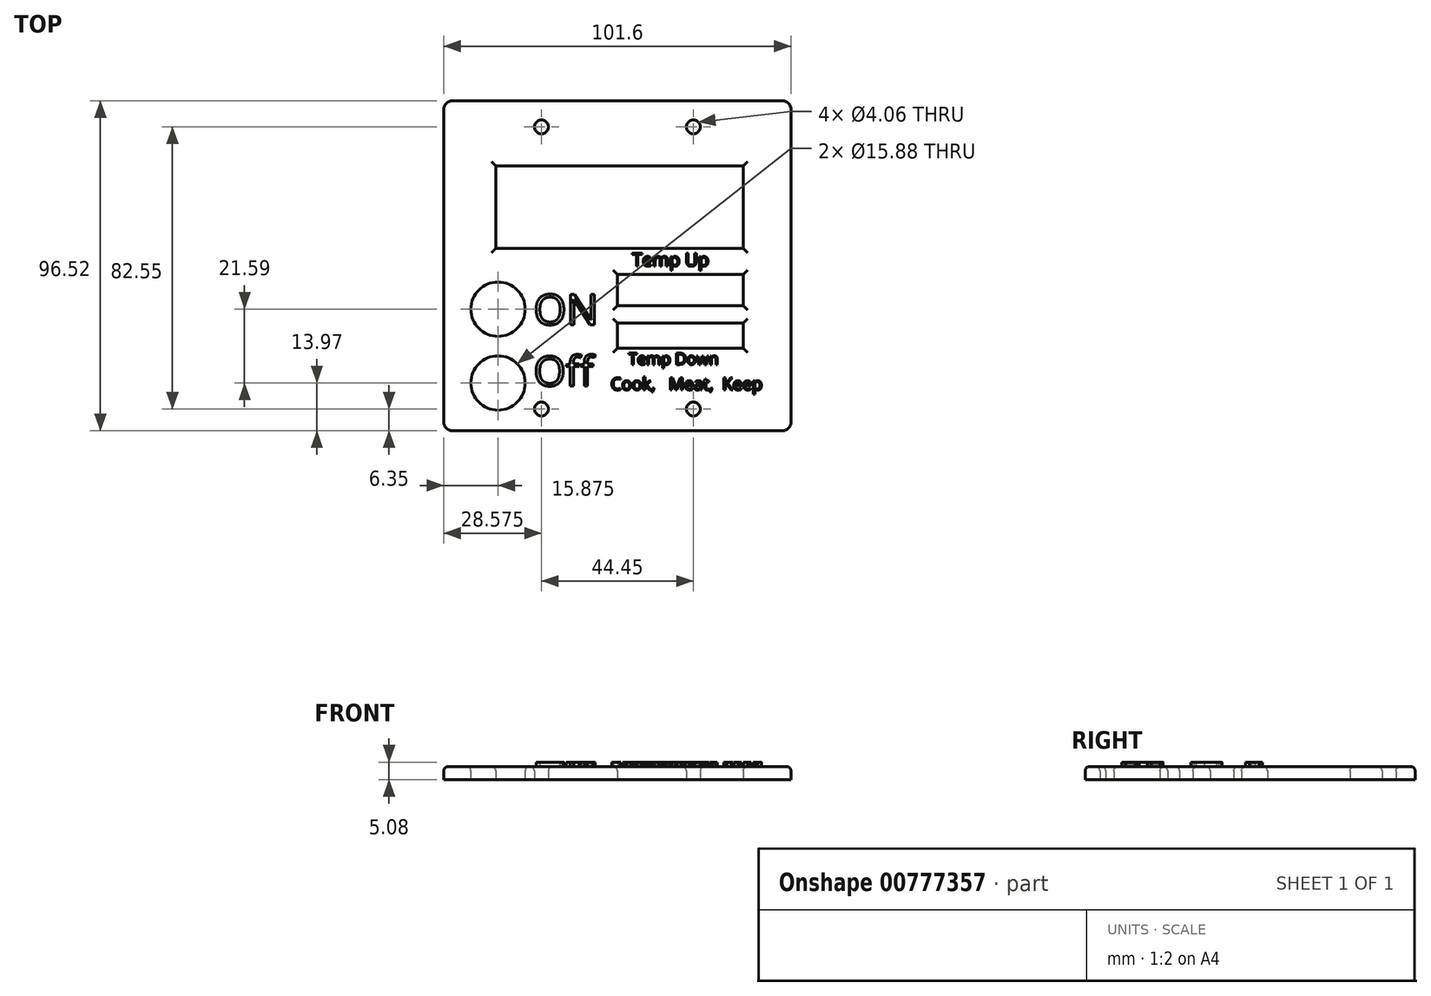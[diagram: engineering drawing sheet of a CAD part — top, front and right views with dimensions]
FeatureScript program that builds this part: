
annotation { "Feature Type Name" : "Feature", "Feature Type Description" : "" }
export const myFeature = defineFeature(function(context is Context, id is Id, definition is map)
    precondition{}
    {
        {
            var Q0;
            Q0=qCreatedBy(makeId("Top.planeOp"),FACE);
            var sketch = newSketch(context, id + "F0", { "sketchPlane" : qUnion([Q0])});
            skLineSegment(sketch, "E0.bottom", {"start": v(0, 0) * mm, "end": v(101.6, 0) * mm});
            skLineSegment(sketch, "E0.top", {"start": v(0, 96.52) * mm, "end": v(101.6, 96.52) * mm});
            skLineSegment(sketch, "E0.left", {"start": v(0, 0) * mm, "end": v(0, 96.52) * mm});
            skLineSegment(sketch, "E0.right", {"start": v(101.6, 0) * mm, "end": v(101.6, 96.52) * mm});
            skCircle(sketch, "E1", {"center": v(28.57, 88.9) * mm, "radius": 2.03 * mm});
            skCircle(sketch, "E2", {"center": v(28.58, 6.35) * mm, "radius": 2.03 * mm});
            skCircle(sketch, "E3", {"center": v(73.03, 6.35) * mm, "radius": 2.03 * mm});
            skCircle(sketch, "E4", {"center": v(73.03, 88.9) * mm, "radius": 2.03 * mm});
            skLineSegment(sketch, "E5.bottom", {"start": v(15.24, 77.47) * mm, "end": v(87.63, 77.47) * mm});
            skLineSegment(sketch, "E5.top", {"start": v(15.24, 53.34) * mm, "end": v(87.63, 53.34) * mm});
            skLineSegment(sketch, "E5.left", {"start": v(15.24, 77.47) * mm, "end": v(15.24, 53.34) * mm});
            skLineSegment(sketch, "E5.right", {"start": v(87.63, 77.47) * mm, "end": v(87.63, 53.34) * mm});
            skCircle(sketch, "E6", {"center": v(15.87, 35.56) * mm, "radius": 7.94 * mm});
            skCircle(sketch, "E7", {"center": v(15.87, 13.97) * mm, "radius": 7.94 * mm});
            skLineSegment(sketch, "E8.bottom", {"start": v(50.8, 45.72) * mm, "end": v(87.63, 45.72) * mm});
            skLineSegment(sketch, "E8.top", {"start": v(50.8, 24.13) * mm, "end": v(87.63, 24.13) * mm});
            skLineSegment(sketch, "E8.left", {"start": v(50.8, 45.72) * mm, "end": v(50.8, 36.58) * mm});
            skLineSegment(sketch, "E8.right", {"start": v(87.63, 45.72) * mm, "end": v(87.63, 36.58) * mm});
            skLineSegment(sketch, "E9", {"start": v(50.8, 36.58) * mm, "end": v(87.63, 36.58) * mm});
            skLineSegment(sketch, "E10", {"start": v(50.8, 31.5) * mm, "end": v(87.63, 31.5) * mm});
            skLineSegment(sketch, "E11.trimOffspring", {"start": v(50.8, 31.5) * mm, "end": v(50.8, 24.13) * mm});
            skLineSegment(sketch, "E12.trimOffspring", {"start": v(87.63, 31.5) * mm, "end": v(87.63, 24.13) * mm});
            skSolve(sketch);
        }
        {
            var Q0;
            Q0 = qSketchRegion(id + "F0", true);
            extrude(context, id + "F1", {"entities" : qUnion([Q0]), "depth" : 3.8 * mm, "offsetDistance" : 25.4 * mm});
        }
        {
            var Q0;
            Q0=makeQuery(id+"F1.opExtrude","SWEPT_EDGE",EDGE,{"disambiguationData":[OSD([sQuery(id+"F0.wireOp",EDGE,"E0.top"),sQuery(id+"F0.wireOp",EDGE,"E0.left")])]});
            var Q1;
            Q1=makeQuery(id+"F1.opExtrude","SWEPT_EDGE",EDGE,{"disambiguationData":[OSD([sQuery(id+"F0.wireOp",EDGE,"E0.bottom"),sQuery(id+"F0.wireOp",EDGE,"E0.left")])]});
            var Q2;
            Q2=makeQuery(id+"F1.opExtrude","SWEPT_EDGE",EDGE,{"disambiguationData":[OSD([sQuery(id+"F0.wireOp",EDGE,"E0.bottom"),sQuery(id+"F0.wireOp",EDGE,"E0.right")])]});
            var Q3;
            Q3=makeQuery(id+"F1.opExtrude","SWEPT_EDGE",EDGE,{"disambiguationData":[OSD([sQuery(id+"F0.wireOp",EDGE,"E0.top"),sQuery(id+"F0.wireOp",EDGE,"E0.right")])]});
            fillet(context, id + "F2", {"entities" : qUnion([Q0, Q1, Q2, Q3]), "radius" : 2.54 * mm, "tangentPropagation" : true, "allowEdgeOverflow" : false});
        }
        {
            var Q0;
            Q0=makeQuery(id+"F1.opExtrude","CAP_EDGE",EDGE,{"disambiguationData":[OSD([sQuery(id+"F0.wireOp",EDGE,"E1")])],"isStart":false});
            var Q1;
            Q1=makeQuery(id+"F1.opExtrude","CAP_EDGE",EDGE,{"disambiguationData":[OSD([sQuery(id+"F0.wireOp",EDGE,"E4")])],"isStart":false});
            var Q2;
            Q2=makeQuery(id+"F1.opExtrude","CAP_EDGE",EDGE,{"disambiguationData":[OSD([sQuery(id+"F0.wireOp",EDGE,"E3")])],"isStart":false});
            var Q3;
            Q3=makeQuery(id+"F1.opExtrude","CAP_EDGE",EDGE,{"disambiguationData":[OSD([sQuery(id+"F0.wireOp",EDGE,"E2")])],"isStart":false});
            fillet(context, id + "F3", {"entities" : qUnion([Q0, Q1, Q2, Q3]), "radius" : 1.27 * mm, "tangentPropagation" : true, "allowEdgeOverflow" : false});
        }
        {
            var Q0;
            Q0=makeQuery(id+"F1.opExtrude","CAP_FACE",FACE,{"disambiguationData":[OSD([sQuery(id+"F0.wireOp",EDGE,"E0.bottom"),sQuery(id+"F0.wireOp",EDGE,"E0.top"),sQuery(id+"F0.wireOp",EDGE,"E0.left"),sQuery(id+"F0.wireOp",EDGE,"E0.right"),sQuery(id+"F0.wireOp",EDGE,"E1"),sQuery(id+"F0.wireOp",EDGE,"E2"),sQuery(id+"F0.wireOp",EDGE,"E3"),sQuery(id+"F0.wireOp",EDGE,"E4"),sQuery(id+"F0.wireOp",EDGE,"E5.bottom"),sQuery(id+"F0.wireOp",EDGE,"E5.top"),sQuery(id+"F0.wireOp",EDGE,"E5.left"),sQuery(id+"F0.wireOp",EDGE,"E5.right"),sQuery(id+"F0.wireOp",EDGE,"E6"),sQuery(id+"F0.wireOp",EDGE,"E7"),sQuery(id+"F0.wireOp",EDGE,"E8.bottom"),sQuery(id+"F0.wireOp",EDGE,"E8.top"),sQuery(id+"F0.wireOp",EDGE,"E8.left"),sQuery(id+"F0.wireOp",EDGE,"E8.right"),sQuery(id+"F0.wireOp",EDGE,"E9"),sQuery(id+"F0.wireOp",EDGE,"E10"),sQuery(id+"F0.wireOp",EDGE,"E11.trimOffspring"),sQuery(id+"F0.wireOp",EDGE,"E12.trimOffspring")])],"isStart":false});
            fillet(context, id + "F4", {"entities" : qUnion([Q0]), "radius" : 1.27 * mm, "tangentPropagation" : true, "allowEdgeOverflow" : false});
        }
        {
            var Q0;
            Q0=makeQuery(id+"F1.opExtrude","CAP_FACE",FACE,{"disambiguationData":[OSD([sQuery(id+"F0.wireOp",EDGE,"E0.bottom"),sQuery(id+"F0.wireOp",EDGE,"E0.top"),sQuery(id+"F0.wireOp",EDGE,"E0.left"),sQuery(id+"F0.wireOp",EDGE,"E0.right"),sQuery(id+"F0.wireOp",EDGE,"E1"),sQuery(id+"F0.wireOp",EDGE,"E2"),sQuery(id+"F0.wireOp",EDGE,"E3"),sQuery(id+"F0.wireOp",EDGE,"E4"),sQuery(id+"F0.wireOp",EDGE,"E5.bottom"),sQuery(id+"F0.wireOp",EDGE,"E5.top"),sQuery(id+"F0.wireOp",EDGE,"E5.left"),sQuery(id+"F0.wireOp",EDGE,"E5.right"),sQuery(id+"F0.wireOp",EDGE,"E6"),sQuery(id+"F0.wireOp",EDGE,"E7"),sQuery(id+"F0.wireOp",EDGE,"E8.bottom"),sQuery(id+"F0.wireOp",EDGE,"E8.top"),sQuery(id+"F0.wireOp",EDGE,"E8.left"),sQuery(id+"F0.wireOp",EDGE,"E8.right"),sQuery(id+"F0.wireOp",EDGE,"E9"),sQuery(id+"F0.wireOp",EDGE,"E10"),sQuery(id+"F0.wireOp",EDGE,"E11.trimOffspring"),sQuery(id+"F0.wireOp",EDGE,"E12.trimOffspring")])],"isStart":false});
            var sketch = newSketch(context, id + "F5", { "sketchPlane" : qUnion([Q0])});
            skText(sketch, "E13", { "text": "Temp Up", "fontName": "OpenSans-Regular.ttf"});
            skText(sketch, "E14", { "text": "Temp Down", "fontName": "OpenSans-Regular.ttf"});
            skText(sketch, "E15", { "text": "ON", "fontName": "OpenSans-Regular.ttf"});
            skText(sketch, "E16", { "text": "Off", "fontName": "OpenSans-Regular.ttf"});
            skText(sketch, "E17", { "text": "Cook,   Meat,  Keep", "fontName": "OpenSans-Regular.ttf"});
            const initialGuessF5  = {"E13": [0.05514, 0.04813, 1, 0, 0.0038], "E14": [0.05401, 0.01937, 1, 0, 0.00337], "E15": [0.02628, 0.03103, 1, 0, 0.0089], "E16": [0.02628, 0.01311, 1, 0, 0.0087], "E17": [0.04886, 0.01192, 1, 0, 0.0036]};
            skSetInitialGuess(sketch, initialGuessF5);
            skSolve(sketch);
        }
        {
            var Q0;
            Q0 = qSketchRegion(id + "F5", true);
            extrude(context, id + "F6", {"entities" : qUnion([Q0]), "operationType" : NewBodyOperationType.ADD, "depth" : 1.27 * mm, "offsetDistance" : 25.4 * mm});
        }
    });
